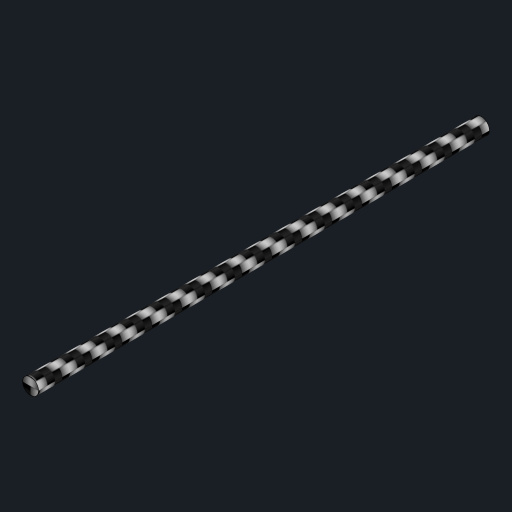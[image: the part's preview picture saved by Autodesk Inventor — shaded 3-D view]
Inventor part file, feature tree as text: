
AUTODESK INVENTOR PART (.ipt)
format: ipt  version: 2023 (Build 270158000, 158)  size: 104,448 bytes
history: native  units: in
note: dims shown in document units (in); Inventor stores cm internally (conversion verified against a paired STEP export)
features: other x1, extrude x1, sketch x1
ambient origin geometry x8: Origin, YZ Plane, XZ Plane, XY Plane, X Axis, Y Axis, Z Axis, Center Point
bodies: Body1 (feature_tree)
feature tree (3):
  other  "ソリッド1"
  extrude  "押し出し1"  Depth=0.0787in
  sketch  "スケッチ1"
